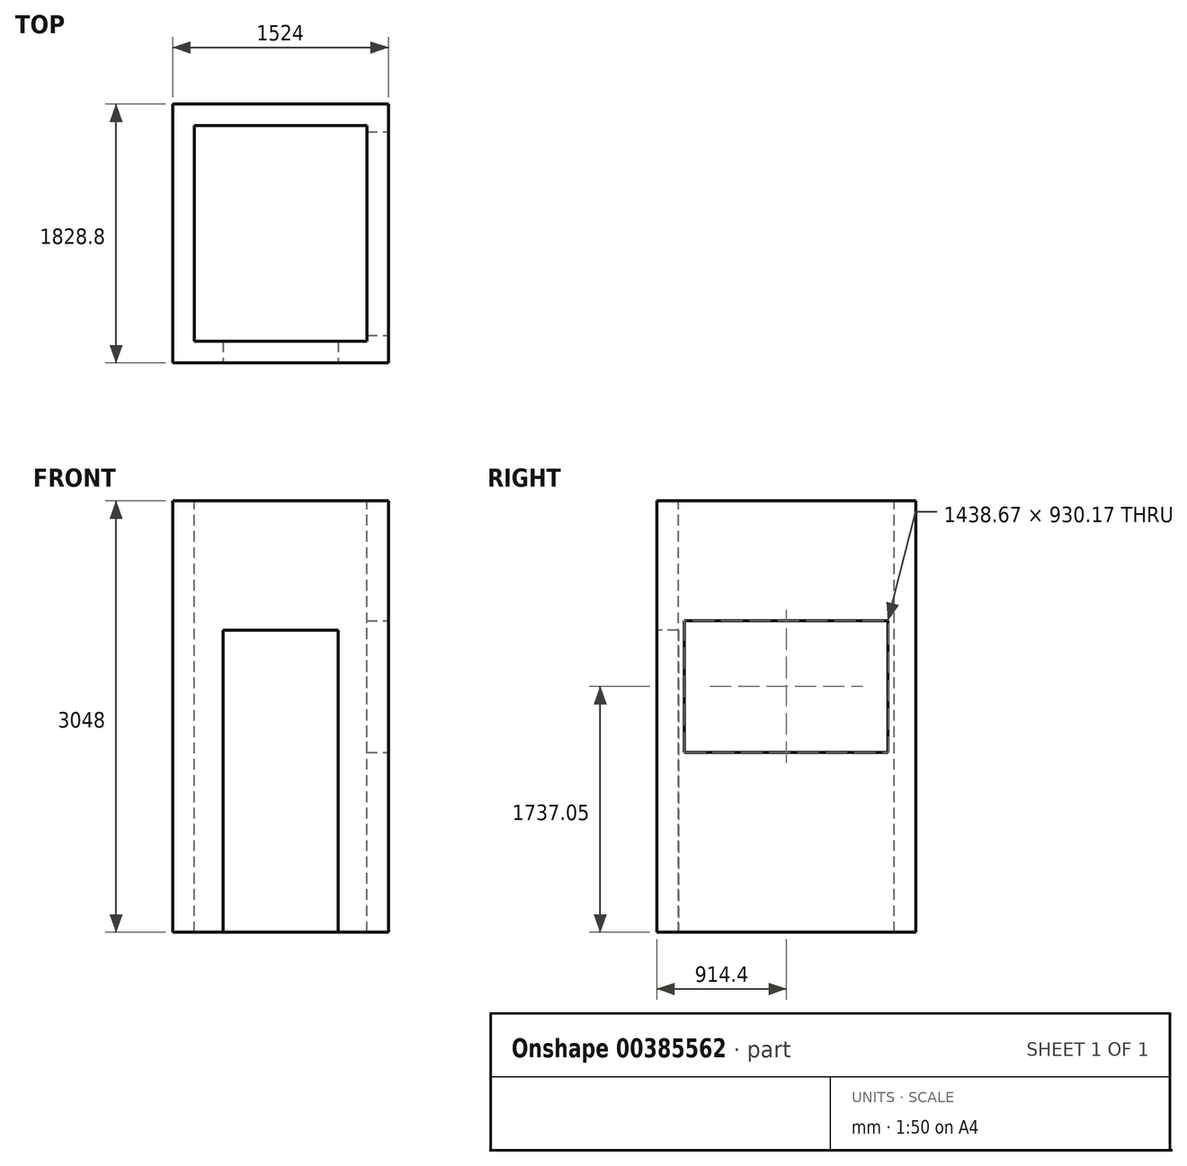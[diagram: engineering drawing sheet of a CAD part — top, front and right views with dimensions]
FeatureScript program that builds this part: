
annotation { "Feature Type Name" : "Feature", "Feature Type Description" : "" }
export const myFeature = defineFeature(function(context is Context, id is Id, definition is map)
    precondition{}
    {
        {
            var Q0;
            Q0=qCreatedBy(makeId("Top.planeOp"),FACE);
            var sketch = newSketch(context, id + "F0", { "sketchPlane" : qUnion([Q0])});
            skLineSegment(sketch, "E0.bottom", {"start": v(762, -914.4) * mm, "end": v(-762, -914.4) * mm});
            skLineSegment(sketch, "E0.top", {"start": v(762, 914.4) * mm, "end": v(-762, 914.4) * mm});
            skLineSegment(sketch, "E0.left", {"start": v(762, -914.4) * mm, "end": v(762, 914.4) * mm});
            skLineSegment(sketch, "E0.right", {"start": v(-762, -914.4) * mm, "end": v(-762, 914.4) * mm});
            skPoint(sketch, "E0.middle", {"position": v(0, 0) * mm});
            skSolve(sketch);
        }
        {
            var Q0;
            Q0 = qSketchRegion(id + "F0", true);
            extrude(context, id + "F1", {"entities" : qUnion([Q0]), "depth" : 3048 * mm});
        }
        {
            var Q0;
            Q0=makeQuery(id+"F1.opExtrude","CAP_FACE",FACE,{"disambiguationData":[OSD([sQuery(id+"F0.wireOp",EDGE,"E0.bottom"),sQuery(id+"F0.wireOp",EDGE,"E0.top"),sQuery(id+"F0.wireOp",EDGE,"E0.left"),sQuery(id+"F0.wireOp",EDGE,"E0.right")])],"isStart":false});
            var sketch = newSketch(context, id + "F2", { "sketchPlane" : qUnion([Q0])});
            skLineSegment(sketch, "E1.0", {"start": v(609.6, -762) * mm, "end": v(609.6, 762) * mm});
            skLineSegment(sketch, "E1.1", {"start": v(-609.6, -762) * mm, "end": v(609.6, -762) * mm});
            skLineSegment(sketch, "E1.2", {"start": v(-609.6, 762) * mm, "end": v(-609.6, -762) * mm});
            skLineSegment(sketch, "E1.3", {"start": v(609.6, 762) * mm, "end": v(-609.6, 762) * mm});
            skSolve(sketch);
        }
        {
            var Q0;
            Q0 = qSketchRegion(id + "F2", true);
            extrude(context, id + "F3", {"entities" : qUnion([Q0]), "operationType" : NewBodyOperationType.REMOVE, "oppositeDirection" : true, "depth" : 3048 * mm});
        }
        {
            var Q0;
            Q0=makeQuery(id+"F1.opExtrude","SWEPT_FACE",FACE,{"disambiguationData":[OSD([sQuery(id+"F0.wireOp",EDGE,"E0.bottom")])]});
            var sketch = newSketch(context, id + "F4", { "sketchPlane" : qUnion([Q0])});
            skLineSegment(sketch, "E2.bottom", {"start": v(406.4, 2133.6) * mm, "end": v(-406.4, 2133.6) * mm});
            skLineSegment(sketch, "E2.top", {"start": v(406.4, -2133.6) * mm, "end": v(-406.4, -2133.6) * mm});
            skLineSegment(sketch, "E2.left", {"start": v(406.4, 2133.6) * mm, "end": v(406.4, -2133.6) * mm});
            skLineSegment(sketch, "E2.right", {"start": v(-406.4, 2133.6) * mm, "end": v(-406.4, -2133.6) * mm});
            skPoint(sketch, "E2.middle", {"position": v(0, 0) * mm});
            skSolve(sketch);
        }
        {
            var Q0;
            {var subQ0=sQuery(id+"F4.wireOp",EDGE,"E2.bottom");Q0=makeQuery(id+"F4.imprint","IMPRINT",FACE,{"disambiguationData":[TD([[makeQuery(id+"F4.imprint","IMPRINT",EDGE,{"derivedFrom":subQ0}),1.0]])]});}
            extrude(context, id + "F5", {"entities" : qUnion([Q0]), "operationType" : NewBodyOperationType.REMOVE, "oppositeDirection" : true, "depth" : 203.2 * mm});
        }
        {
            var Q0;
            Q0=makeQuery(id+"F1.opExtrude","SWEPT_FACE",FACE,{"disambiguationData":[OSD([sQuery(id+"F0.wireOp",EDGE,"E0.left")])]});
            var sketch = newSketch(context, id + "F6", { "sketchPlane" : qUnion([Q0])});
            skLineSegment(sketch, "E3.bottom", {"start": v(719.33, 1271.96) * mm, "end": v(-719.33, 1271.96) * mm});
            skLineSegment(sketch, "E3.top", {"start": v(719.33, 2202.13) * mm, "end": v(-719.33, 2202.13) * mm});
            skLineSegment(sketch, "E3.left", {"start": v(719.33, 1271.96) * mm, "end": v(719.33, 2202.13) * mm});
            skLineSegment(sketch, "E3.right", {"start": v(-719.33, 1271.96) * mm, "end": v(-719.33, 2202.13) * mm});
            skPoint(sketch, "E3.middle", {"position": v(0, 1737.05) * mm});
            skSolve(sketch);
        }
        {
            var Q0;
            Q0=makeQuery(id+"F6.imprint","IMPRINT",FACE,{"disambiguationData":[TD([[makeQuery(id+"F6.imprint","IMPRINT",EDGE,{"derivedFrom":sQuery(id+"F6.wireOp",EDGE,"E3.bottom")}),-1.0]])]});
            extrude(context, id + "F7", {"entities" : qUnion([Q0]), "operationType" : NewBodyOperationType.REMOVE, "oppositeDirection" : true, "depth" : 203.2 * mm});
        }
    });
